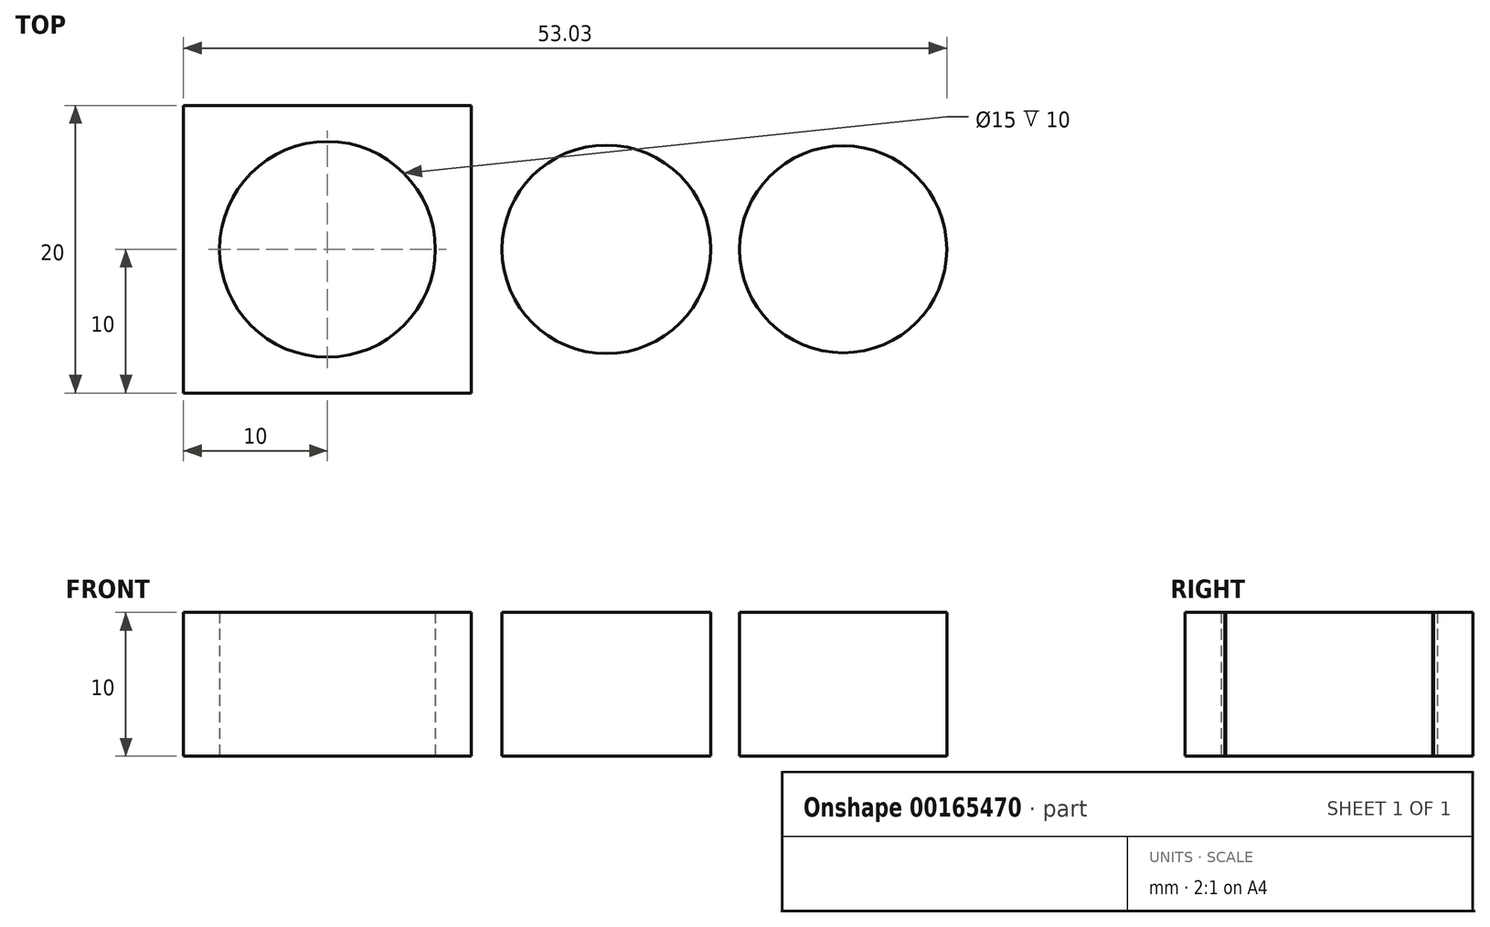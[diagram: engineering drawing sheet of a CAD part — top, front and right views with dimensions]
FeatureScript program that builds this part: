
annotation { "Feature Type Name" : "Feature", "Feature Type Description" : "" }
export const myFeature = defineFeature(function(context is Context, id is Id, definition is map)
    precondition{}
    {
        {
            var Q0;
            Q0=qCreatedBy(makeId("Top.planeOp"),FACE);
            var sketch = newSketch(context, id + "F0", { "sketchPlane" : qUnion([Q0])});
            skCircle(sketch, "E0", {"center": v(0, 0) * mm, "radius": 7.5 * mm});
            skLineSegment(sketch, "E1.bottom", {"start": v(-10, -10) * mm, "end": v(10, -10) * mm});
            skLineSegment(sketch, "E1.top", {"start": v(-10, 10) * mm, "end": v(10, 10) * mm});
            skLineSegment(sketch, "E1.left", {"start": v(-10, -10) * mm, "end": v(-10, 10) * mm});
            skLineSegment(sketch, "E1.right", {"start": v(10, -10) * mm, "end": v(10, 10) * mm});
            skCircle(sketch, "E2", {"center": v(19.38, 0) * mm, "radius": 7.25 * mm});
            skCircle(sketch, "E3", {"center": v(35.83, 0) * mm, "radius": 7.2 * mm});
            skSolve(sketch);
        }
        {
            var Q0;
            Q0=makeQuery(id+"F0.imprint","IMPRINT",FACE,{"disambiguationData":[TD([[makeQuery(id+"F0.imprint","IMPRINT",EDGE,{"derivedFrom":sQuery(id+"F0.wireOp",EDGE,"E0")}),-1.0]])]});
            var Q1;
            Q1=makeQuery(id+"F0.imprint","IMPRINT",FACE,{"disambiguationData":[TD([[makeQuery(id+"F0.imprint","IMPRINT",EDGE,{"derivedFrom":sQuery(id+"F0.wireOp",EDGE,"rkz7lJM7-XaLU-7umj-0thS-jZc0StsTudxY")}),1.0]])]});
            var Q2;
            Q2=makeQuery(id+"F0.imprint","IMPRINT",FACE,{"disambiguationData":[TD([[makeQuery(id+"F0.imprint","IMPRINT",EDGE,{"derivedFrom":sQuery(id+"F0.wireOp",EDGE,"F3XrmDRp-jQmh-nvlw-pT96-XMXBfB0CPq9m")}),1.0]])]});
            var Q3;
            Q3=makeQuery(id+"F0.imprint","IMPRINT",FACE,{"disambiguationData":[TD([[makeQuery(id+"F0.imprint","IMPRINT",EDGE,{"derivedFrom":sQuery(id+"F0.wireOp",EDGE,"E3")}),1.0]])]});
            var Q4;
            Q4=makeQuery(id+"F0.imprint","IMPRINT",FACE,{"disambiguationData":[TD([[makeQuery(id+"F0.imprint","IMPRINT",EDGE,{"derivedFrom":sQuery(id+"F0.wireOp",EDGE,"E2")}),1.0]])]});
            extrude(context, id + "F1", {"entities" : qUnion([Q0, Q1, Q2, Q3, Q4]), "depth" : 10 * mm, "offsetDistance" : 25 * mm});
        }
    });
